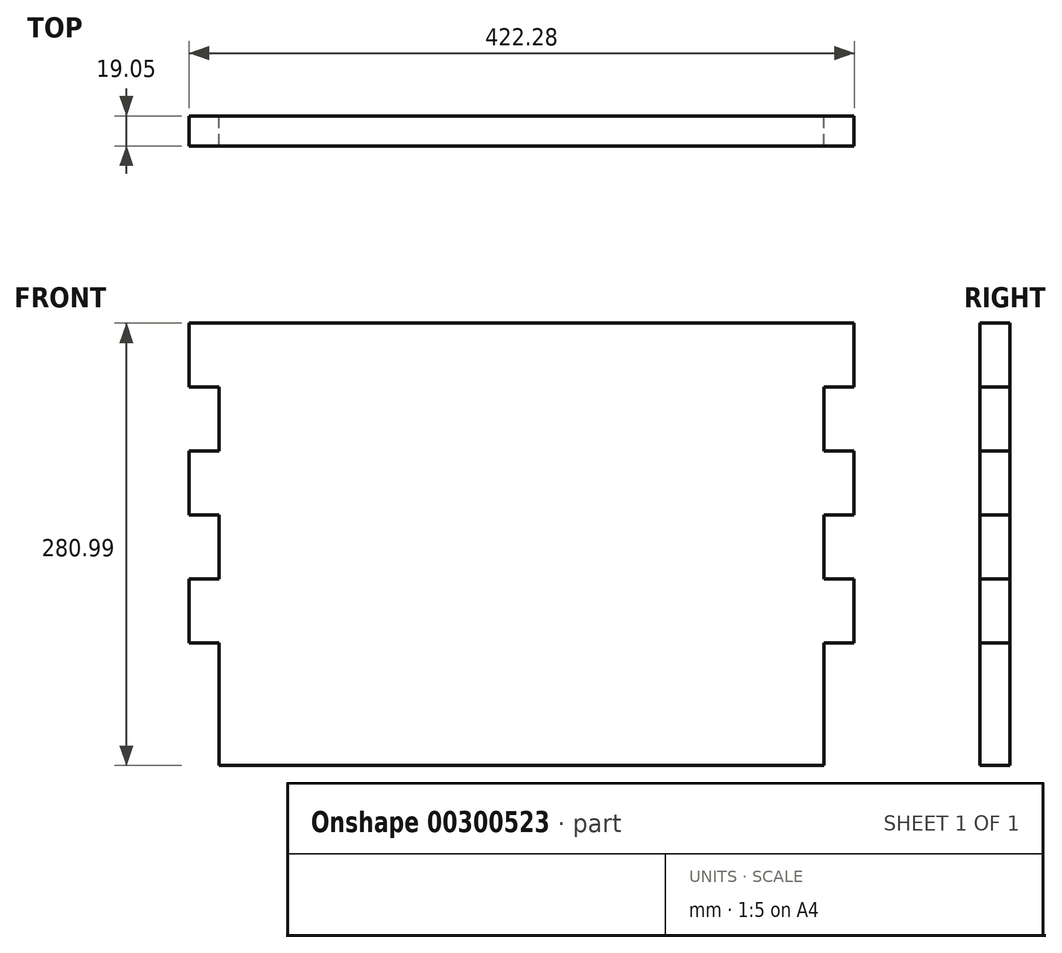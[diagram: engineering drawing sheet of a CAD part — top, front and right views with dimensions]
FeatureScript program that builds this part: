
annotation { "Feature Type Name" : "Feature", "Feature Type Description" : "" }
export const myFeature = defineFeature(function(context is Context, id is Id, definition is map)
    precondition{}
    {
        {
            var Q0;
            Q0=qCreatedBy(makeId("Front.planeOp"),FACE);
            var sketch = newSketch(context, id + "F0", { "sketchPlane" : qUnion([Q0])});
            skLineSegment(sketch, "E0.top", {"start": v(-193.16, 63.84) * mm, "end": v(-174.1, 63.84) * mm});
            skLineSegment(sketch, "E0.left", {"start": v(-193.16, 104.48) * mm, "end": v(-193.16, 63.84) * mm});
            skLineSegment(sketch, "E1.0.1.0", {"start": v(-193.16, 23.2) * mm, "end": v(-174.1, 23.2) * mm});
            skLineSegment(sketch, "E1.0.1.1", {"start": v(-174.1, 63.84) * mm, "end": v(-174.1, 23.2) * mm});
            skLineSegment(sketch, "E1.0.2.0", {"start": v(-193.16, -17.44) * mm, "end": v(-174.1, -17.44) * mm});
            skLineSegment(sketch, "E1.0.2.2", {"start": v(-193.16, 23.2) * mm, "end": v(-193.16, -17.44) * mm});
            skLineSegment(sketch, "E1.0.2.3", {"start": v(-193.16, 23.2) * mm, "end": v(-174.1, 23.2) * mm});
            skLineSegment(sketch, "E1.0.3.0", {"start": v(-193.16, -58.08) * mm, "end": v(-174.1, -58.08) * mm});
            skLineSegment(sketch, "E1.0.3.1", {"start": v(-174.1, -17.44) * mm, "end": v(-174.1, -58.08) * mm});
            skLineSegment(sketch, "E1.0.3.3", {"start": v(-193.16, -17.44) * mm, "end": v(-174.1, -17.44) * mm});
            skLineSegment(sketch, "E1.0.4.0", {"start": v(-193.16, -98.72) * mm, "end": v(-174.1, -98.72) * mm});
            skLineSegment(sketch, "E1.0.4.2", {"start": v(-193.16, -58.08) * mm, "end": v(-193.16, -98.72) * mm});
            skLineSegment(sketch, "E1.0.4.3", {"start": v(-193.16, -58.08) * mm, "end": v(-174.1, -58.08) * mm});
            skLineSegment(sketch, "E1.0.5.3", {"start": v(-193.16, -98.72) * mm, "end": v(-174.1, -98.72) * mm});
            skLineSegment(sketch, "E2", {"start": v(-174.1, -98.72) * mm, "end": v(-174.1, -138.4) * mm});
            skLineSegment(sketch, "E3", {"start": v(-193.16, 104.48) * mm, "end": v(17.98, 104.48) * mm});
            skLineSegment(sketch, "E4", {"start": v(-174.1, -138.4) * mm, "end": v(17.98, -138.4) * mm});
            skLineSegment(sketch, "E5.MirrorCS", {"start": v(229.12, 63.84) * mm, "end": v(210.07, 63.84) * mm});
            skLineSegment(sketch, "E6.MirrorCS", {"start": v(229.12, -58.08) * mm, "end": v(210.07, -58.08) * mm});
            skLineSegment(sketch, "E7.MirrorCS", {"start": v(229.12, 23.2) * mm, "end": v(210.07, 23.2) * mm});
            skLineSegment(sketch, "E8.MirrorCS", {"start": v(229.12, -98.72) * mm, "end": v(210.07, -98.72) * mm});
            skLineSegment(sketch, "E9.MirrorCS", {"start": v(229.12, -17.44) * mm, "end": v(210.07, -17.44) * mm});
            skLineSegment(sketch, "E10.MirrorCS", {"start": v(210.07, -98.72) * mm, "end": v(210.07, -138.4) * mm});
            skLineSegment(sketch, "E11.MirrorCS", {"start": v(229.12, -58.08) * mm, "end": v(229.12, -98.72) * mm});
            skLineSegment(sketch, "E12.MirrorCS", {"start": v(229.12, 104.48) * mm, "end": v(229.12, 63.84) * mm});
            skLineSegment(sketch, "E13.MirrorCS", {"start": v(229.12, 23.2) * mm, "end": v(229.12, -17.44) * mm});
            skLineSegment(sketch, "E14.MirrorCS", {"start": v(210.07, -17.44) * mm, "end": v(210.07, -58.08) * mm});
            skLineSegment(sketch, "E15.MirrorCS", {"start": v(210.07, 63.84) * mm, "end": v(210.07, 23.2) * mm});
            skLineSegment(sketch, "E16.MirrorCS", {"start": v(210.07, -138.4) * mm, "end": v(17.98, -138.4) * mm});
            skLineSegment(sketch, "E17.MirrorCS", {"start": v(229.12, 104.48) * mm, "end": v(17.98, 104.48) * mm});
            skSolve(sketch);
        }
        {
            var Q0;
            Q0=qSketchRegion(id+"F0",true);
            extrude(context, id + "F1", {"entities" : qUnion([Q0]), "depth" : 19.05 * mm});
        }
        {
            var Q0;
            Q0=makeQuery(id+"F1.opExtrude","SWEPT_FACE",FACE,{"disambiguationData":[OSD([sQuery(id+"F0.wireOp",EDGE,"E4"),sQuery(id+"F0.wireOp",EDGE,"E16.MirrorCS")])]});
            var sketch = newSketch(context, id + "F2", { "sketchPlane" : qUnion([Q0])});
            skLineSegment(sketch, "E18.bottom", {"start": v(-174.1, 19.05) * mm, "end": v(210.07, 19.05) * mm});
            skLineSegment(sketch, "E18.top", {"start": v(-174.1, 0) * mm, "end": v(210.07, 0) * mm});
            skLineSegment(sketch, "E18.left", {"start": v(-174.1, 19.05) * mm, "end": v(-174.1, 0) * mm});
            skLineSegment(sketch, "E18.right", {"start": v(210.07, 19.05) * mm, "end": v(210.07, 0) * mm});
            skSolve(sketch);
        }
        {
            var Q0;
            Q0=makeQuery(id+"F2.imprint","IMPRINT",FACE,{"disambiguationData":[TD([[makeQuery(id+"F2.imprint","IMPRINT",EDGE,{"derivedFrom":sQuery(id+"F2.wireOp",EDGE,"E18.bottom")}),-1.0]])]});
            extrude(context, id + "F3", {"entities" : qUnion([Q0]), "operationType" : NewBodyOperationType.ADD, "depth" : 38.1 * mm});
        }
    });
